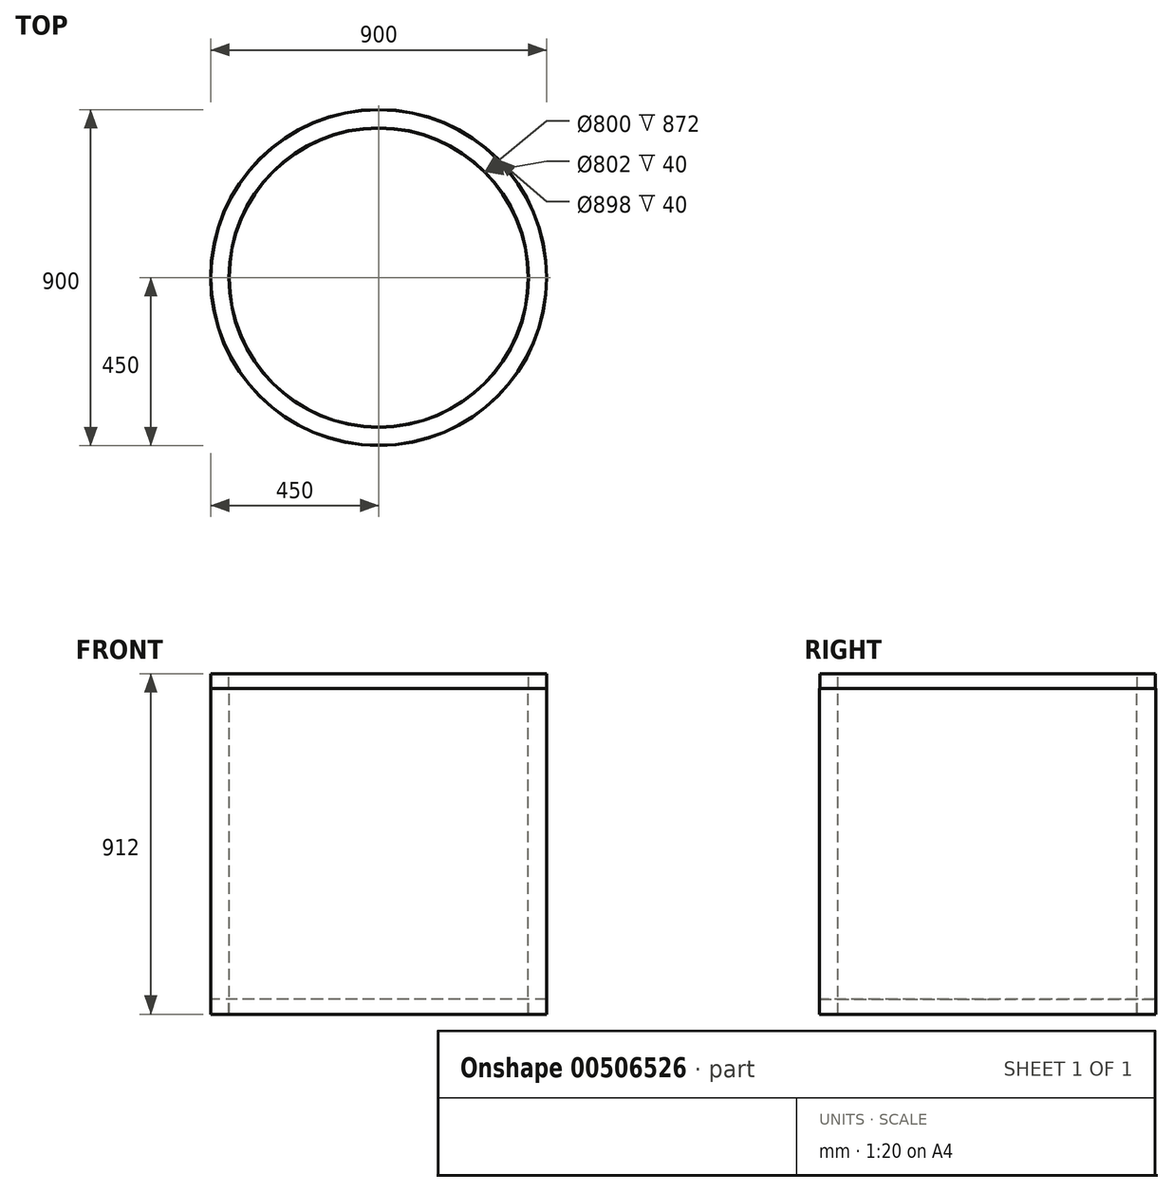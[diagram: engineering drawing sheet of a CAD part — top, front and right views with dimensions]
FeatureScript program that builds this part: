
annotation { "Feature Type Name" : "Feature", "Feature Type Description" : "" }
export const myFeature = defineFeature(function(context is Context, id is Id, definition is map)
    precondition{}
    {
        {
            var Q0;
            Q0=qCreatedBy(makeId("Front.planeOp"),FACE);
            var sketch = newSketch(context, id + "F0", { "sketchPlane" : qUnion([Q0])});
            skLineSegment(sketch, "E0", {"start": v(0, 74.87) * mm, "end": v(0, -73.71) * mm, "construction": true});
            skLineSegment(sketch, "E1", {"start": v(0, 374.84) * mm, "end": v(0, -528.94) * mm, "construction": true});
            skLineSegment(sketch, "E2", {"start": v(-400, -489.75) * mm, "end": v(-400, 382.25) * mm});
            skLineSegment(sketch, "E3", {"start": v(-400, 382.25) * mm, "end": v(-401, 382.25) * mm});
            skLineSegment(sketch, "E4", {"start": v(-401, 382.25) * mm, "end": v(-401, 422.25) * mm});
            skLineSegment(sketch, "E5", {"start": v(-401, 422.25) * mm, "end": v(-449, 422.25) * mm});
            skLineSegment(sketch, "E6", {"start": v(-449, 422.25) * mm, "end": v(-449, 382.25) * mm});
            skLineSegment(sketch, "E7", {"start": v(-449, 382.25) * mm, "end": v(-450, 382.25) * mm});
            skLineSegment(sketch, "E8", {"start": v(-450, 382.25) * mm, "end": v(-450, -489.75) * mm});
            skLineSegment(sketch, "E9", {"start": v(-450, -489.75) * mm, "end": v(-449, -489.75) * mm});
            skLineSegment(sketch, "E10", {"start": v(-449, -489.75) * mm, "end": v(-449, -449.75) * mm});
            skLineSegment(sketch, "E11", {"start": v(-449, -449.75) * mm, "end": v(-401, -449.75) * mm});
            skLineSegment(sketch, "E12", {"start": v(-401, -449.75) * mm, "end": v(-401, -489.75) * mm});
            skLineSegment(sketch, "E13", {"start": v(-401, -489.75) * mm, "end": v(-400, -489.75) * mm});
            skSolve(sketch);
        }
        {
            var Q0;
            Q0=qSketchRegion(id+"F0",true);
            var Q1;
            Q1=sQuery(id+"F0.wireOp",EDGE,"E1");
            revolve(context, id + "F1", {"entities" : qUnion([Q0]), "axis" : qUnion([Q1]), "revolveType" : RevolveType.FULL});
        }
    });
